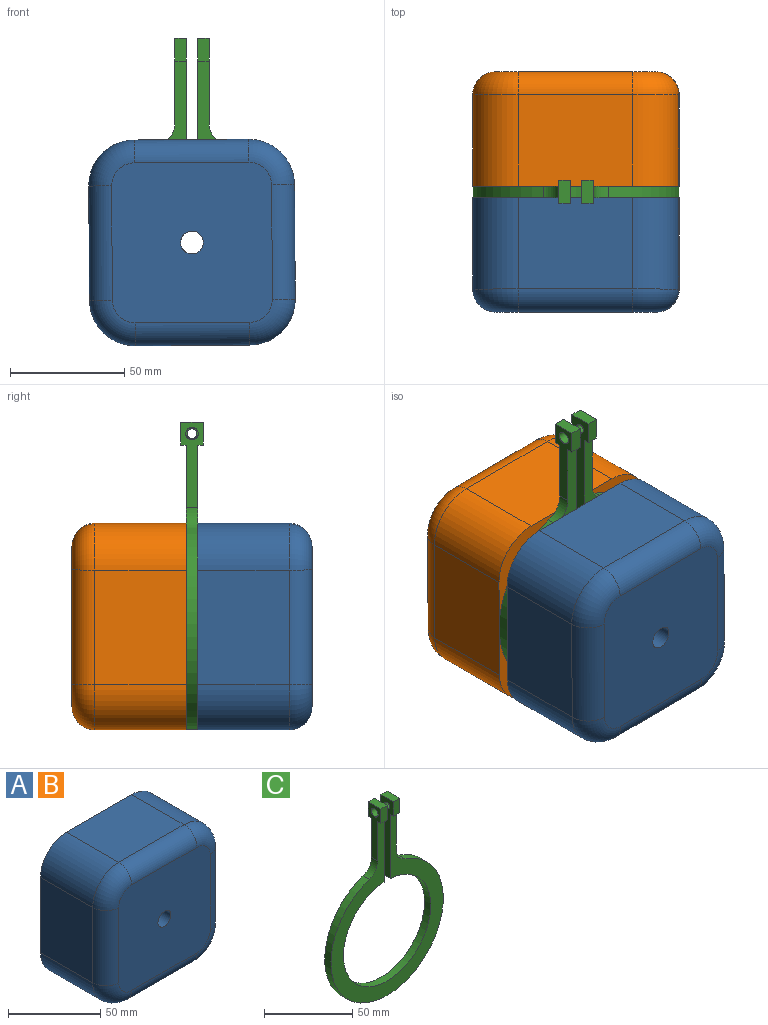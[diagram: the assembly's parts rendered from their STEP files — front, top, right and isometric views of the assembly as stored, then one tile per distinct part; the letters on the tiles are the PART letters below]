
ASSEMBLY  parts=3 mates=5
PART A: 19 faces, bbox 93.3x50x93.3 mm
  f0: plane 50x40mm, normal (0,0,1), area 2000mm2, adj f6,f7,f10,f14
  f1: plane 50x40mm, normal (-1,0,0), area 2000mm2, adj f6,f7,f8,f18
  f2: plane 50x40mm, normal (0,0,-1), area 2000mm2, adj f6,f8,f9,f15
  f3: cylinder r=5mm len=50mm, axis (0,1,0), area 1570.8mm2, adj f5,f6
  f4: plane 50x40mm, normal (1,0,0), area 2000mm2, adj f6,f9,f10,f11
  f5: plane 70x70mm, normal (0,-1,0), area 4735.6mm2, adj f3,f11,f12,f13,f14,f15,f16,f17
  f6: plane 90x90mm, normal (0,1,0), area 7678.1mm2, adj f0,f1,f2,f3,f4,f7,f8,f9
  f7: cylinder r=20mm len=40mm, axis (0,-1,0), area 1256.6mm2, adj f0,f1,f6,f16
  f8: cylinder r=20mm len=40mm, axis (0,1,0), area 1256.6mm2, adj f1,f2,f6,f17
  f9: cylinder r=20mm len=40mm, axis (0,-1,0), area 1256.6mm2, adj f2,f4,f6,f13
  f10: cylinder r=20mm len=40mm, axis (0,1,0), area 1256.6mm2, adj f0,f4,f6,f12
  f11: cylinder r=10mm len=50mm, axis (0,0,-1), area 785.4mm2, adj f4,f5,f12,f13
  f12: torus R=10mm, axis (0,-1,0), area 403.8mm2, adj f5,f10,f11,f14
  f13: torus R=10mm, axis (0,-1,0), area 403.8mm2, adj f5,f9,f11,f15
  f14: cylinder r=10mm len=50mm, axis (1,0,0), area 785.4mm2, adj f0,f5,f12,f16
  f15: cylinder r=10mm len=50mm, axis (-1,0,0), area 785.4mm2, adj f2,f5,f13,f17
  f16: torus R=10mm, axis (0,-1,0), area 403.8mm2, adj f5,f7,f14,f18
  f17: torus R=10mm, axis (0,-1,0), area 403.8mm2, adj f5,f8,f15,f18
  f18: cylinder r=10mm len=50mm, axis (0,0,1), area 785.4mm2, adj f1,f5,f16,f17
PART B: same geometry as A
PART C: 22 faces, bbox 90x10x134.4 mm
  f0: cylinder r=45mm len=90mm, axis (0,1,0), area 1268mm2, adj f12,f15,f20,f21
  f1: cylinder r=35mm len=70mm, axis (0,1,0), area 1074.5mm2, adj f5,f6,f12,f15
  f2: plane 10x5mm, normal (0,1,0), area 50mm2, adj f6,f7,f11,f17
  f3: plane 10x5mm, normal (0,1,0), area 50mm2, adj f4,f5,f10,f16
  f4: plane 37.23x10mm, normal (1,0,0), area 222.3mm2, adj f3,f9,f10,f12,f13,f15,f16,f18
  f5: plane 54.46x10mm, normal (-1,0,0), area 308.4mm2, adj f1,f3,f9,f10,f12,f13,f15,f16
  f6: plane 54.46x10mm, normal (1,0,0), area 298.5mm2, adj f1,f2,f8,f11,f12,f14,f15,f17
  f7: plane 37.23x10mm, normal (-1,0,0), area 212.4mm2, adj f2,f8,f11,f12,f14,f15,f17,f19
  f8: plane 10x5mm, normal (0,-1,0), area 50mm2, adj f6,f7,f11,f14
  f9: plane 10x5mm, normal (0,-1,0), area 50mm2, adj f4,f5,f10,f13
  f10: plane 10x5mm, normal (0,0,1), area 50mm2, adj f3,f4,f5,f9
  f11: plane 10x5mm, normal (0,0,1), area 50mm2, adj f2,f6,f7,f8
  f12: plane 124.37x90mm, normal (0,-1,0), area 2831.8mm2, adj f0,f1,f4,f5,f6,f7,f13,f14
  f13: plane 5x2.5mm, normal (0,0,-1), area 12.5mm2, adj f4,f5,f9,f12
  f14: plane 5x2.5mm, normal (0,0,-1), area 12.5mm2, adj f6,f7,f8,f12
  f15: plane 124.37x90mm, normal (0,1,0), area 2831.8mm2, adj f0,f1,f4,f5,f6,f7,f16,f17
  f16: plane 5x2.5mm, normal (0,0,-1), area 12.5mm2, adj f3,f4,f5,f15
  f17: plane 5x2.5mm, normal (0,0,-1), area 12.5mm2, adj f2,f6,f7,f15
  f18: cylinder r=2.1mm len=5mm, axis (-1,0,0), area 66mm2, adj f4,f5
  f19: cylinder r=2.75mm len=5.5mm, axis (1,0,0), area 86.4mm2, adj f6,f7
  f20: cylinder r=10mm len=9.48mm, axis (0,1,0), area 62.3mm2, adj f0,f4,f12,f15
  f21: cylinder r=10mm len=9.48mm, axis (0,1,0), area 62.3mm2, adj f0,f7,f12,f15
PLACE A rot(axis=(0,1,0),89.6deg) t=(-23.89,-16.45,-22.43)mm
PLACE B rot(axis=(0.71,0,-0.7),180deg) t=(-23.89,-11.45,-22.43)mm
PLACE C t=(-23.89,-13.95,-22.43)mm fixed
MATE planar C.f1 <-> A.f3  axis (0,-1,0) through (-23.89,-16.45,-22.43)mm
MATE planar A.f4 <-> B.f4  axis (0.01,0,-1) through (-23.61,-36.45,-67.43)mm
MATE planar B.f3 <-> C.f1  axis (0,-1,0) through (-23.89,-11.45,-22.43)mm
MATE planar B.f0 <-> A.f2  axis (-1,0,-0.01) through (-68.89,8.55,-22.71)mm
MATE cylindrical C.f1 <-> B.f3  axis (0,1,0) through (-23.89,-11.45,-22.43)mm
